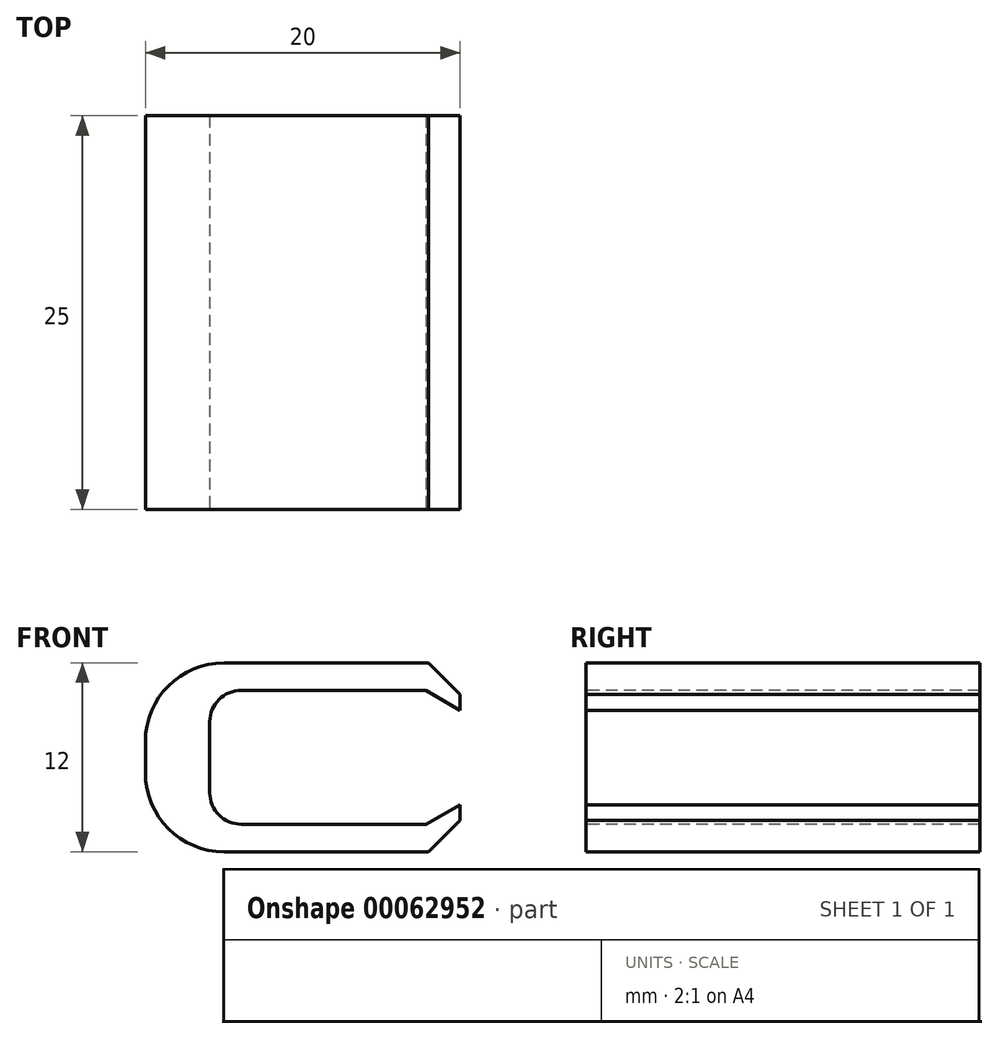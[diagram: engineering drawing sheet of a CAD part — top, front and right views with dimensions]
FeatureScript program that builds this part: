
annotation { "Feature Type Name" : "Feature", "Feature Type Description" : "" }
export const myFeature = defineFeature(function(context is Context, id is Id, definition is map)
    precondition{}
    {
        {
            var Q0;
            Q0=qCreatedBy(makeId("Front.planeOp"),FACE);
            var sketch = newSketch(context, id + "F0", { "sketchPlane" : qUnion([Q0])});
            skLineSegment(sketch, "E0.rect.bottom", {"start": v(-10, 6) * mm, "end": v(10, 6) * mm});
            skLineSegment(sketch, "E0.rect.top", {"start": v(-10, -6) * mm, "end": v(10, -6) * mm});
            skLineSegment(sketch, "E0.rect.left", {"start": v(-10, 6) * mm, "end": v(-10, -6) * mm});
            skLineSegment(sketch, "E0.rect.right", {"start": v(10, 6) * mm, "end": v(10, -6) * mm});
            skPoint(sketch, "E0.rect.middle", {"position": v(0, 0) * mm});
            skSolve(sketch);
        }
        {
            var Q0;
            Q0=makeQuery(id+"F0.imprint","IMPRINT",FACE,{"disambiguationData":[TD([[makeQuery(id+"F0.imprint","IMPRINT",EDGE,{"derivedFrom":sQuery(id+"F0.wireOp",EDGE,"E0.rect.bottom")}),-1.0]])]});
            extrude(context, id + "F1", {"entities" : qUnion([Q0]), "depth" : 25 * mm});
        }
        {
            var Q0;
            Q0=makeQuery(id+"F1.opExtrude","SWEPT_EDGE",EDGE,{"disambiguationData":[OSD([sQuery(id+"F0.wireOp",EDGE,"E0.rect.bottom"),sQuery(id+"F0.wireOp",EDGE,"E0.rect.left")])]});
            var Q1;
            Q1=makeQuery(id+"F1.opExtrude","SWEPT_EDGE",EDGE,{"disambiguationData":[OSD([sQuery(id+"F0.wireOp",EDGE,"E0.rect.top"),sQuery(id+"F0.wireOp",EDGE,"E0.rect.left")])]});
            fillet(context, id + "F2", {"entities" : qUnion([Q0, Q1]), "radius" : 5 * mm, "tangentPropagation" : true, "allowEdgeOverflow" : false});
        }
        {
            var Q0;
            Q0=makeQuery(id+"F1.opExtrude","SWEPT_EDGE",EDGE,{"disambiguationData":[OSD([sQuery(id+"F0.wireOp",EDGE,"E0.rect.bottom"),sQuery(id+"F0.wireOp",EDGE,"E0.rect.right")])]});
            var Q1;
            Q1=makeQuery(id+"F1.opExtrude","SWEPT_EDGE",EDGE,{"disambiguationData":[OSD([sQuery(id+"F0.wireOp",EDGE,"E0.rect.top"),sQuery(id+"F0.wireOp",EDGE,"E0.rect.right")])]});
            chamfer(context, id + "F3", {"entities" : qUnion([Q0, Q1]), "width" : 2 * mm, "tangentPropagation" : true});
        }
        {
            var Q0;
            Q0=makeQuery(id+"F1.opExtrude","CAP_FACE",FACE,{"disambiguationData":[OSD([sQuery(id+"F0.wireOp",EDGE,"E0.rect.bottom"),sQuery(id+"F0.wireOp",EDGE,"E0.rect.top"),sQuery(id+"F0.wireOp",EDGE,"E0.rect.left"),sQuery(id+"F0.wireOp",EDGE,"E0.rect.right")])],"isStart":false});
            var sketch = newSketch(context, id + "F4", { "sketchPlane" : qUnion([Q0])});
            skLineSegment(sketch, "E1", {"start": v(10, 2.97) * mm, "end": v(7.83, 4.25) * mm});
            skLineSegment(sketch, "E2", {"start": v(7.83, 4.25) * mm, "end": v(-5.91, 4.25) * mm});
            skLineSegment(sketch, "E3", {"start": v(-5.91, 4.25) * mm, "end": v(-5.91, -4.25) * mm});
            skLineSegment(sketch, "E4", {"start": v(-5.91, -4.25) * mm, "end": v(7.83, -4.25) * mm});
            skLineSegment(sketch, "E5", {"start": v(7.83, -4.25) * mm, "end": v(10, -3.03) * mm});
            skLineSegment(sketch, "E6", {"start": v(10, -3.03) * mm, "end": v(10, 2.97) * mm});
            skSolve(sketch);
        }
        {
            var Q0;
            Q0=makeQuery(id+"F4.imprint","IMPRINT",FACE,{"disambiguationData":[TD([[makeQuery(id+"F4.imprint","IMPRINT",EDGE,{"derivedFrom":sQuery(id+"F4.wireOp",EDGE,"E1")}),1.0]])]});
            extrude(context, id + "F5", {"entities" : qUnion([Q0]), "operationType" : NewBodyOperationType.REMOVE, "oppositeDirection" : true, "depth" : 25 * mm});
        }
        {
            var Q0;
            Q0=makeQuery(id+"F5.boolean.opBoolean","COPY",EDGE,{"derivedFrom":makeQuery(id+"F5.opExtrude","SWEPT_EDGE",EDGE,{"disambiguationData":[OSD([sQuery(id+"F4.wireOp",EDGE,"E3"),sQuery(id+"F4.wireOp",EDGE,"E4")])]})});
            var Q1;
            Q1=makeQuery(id+"F5.boolean.opBoolean","COPY",EDGE,{"derivedFrom":makeQuery(id+"F5.opExtrude","SWEPT_EDGE",EDGE,{"disambiguationData":[OSD([sQuery(id+"F4.wireOp",EDGE,"E2"),sQuery(id+"F4.wireOp",EDGE,"E3")])]})});
            fillet(context, id + "F6", {"entities" : qUnion([Q0, Q1]), "radius" : 2 * mm, "tangentPropagation" : true, "allowEdgeOverflow" : false});
        }
    });
